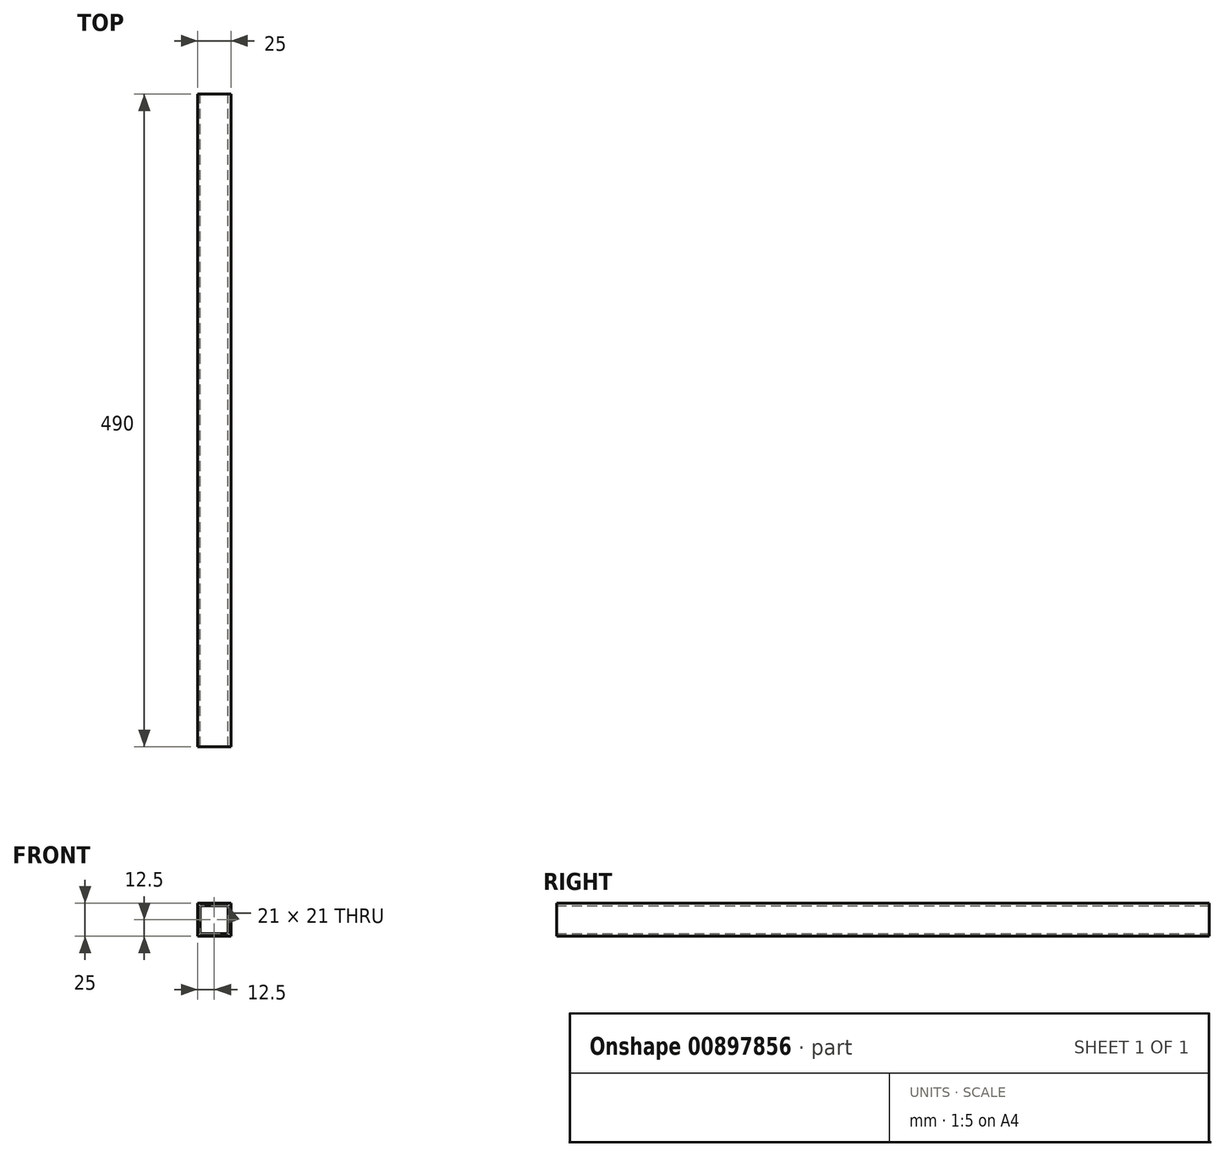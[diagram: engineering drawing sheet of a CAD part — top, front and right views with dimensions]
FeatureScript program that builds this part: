
annotation { "Feature Type Name" : "Feature", "Feature Type Description" : "" }
export const myFeature = defineFeature(function(context is Context, id is Id, definition is map)
    precondition{}
    {
        {
            var Q0;
            Q0=qCreatedBy(makeId("Front.planeOp"),FACE);
            var sketch = newSketch(context, id + "F0", { "sketchPlane" : qUnion([Q0])});
            skLineSegment(sketch, "E0.bottom", {"start": v(12.5, -12.5) * mm, "end": v(-12.5, -12.5) * mm});
            skLineSegment(sketch, "E0.top", {"start": v(12.5, 12.5) * mm, "end": v(-12.5, 12.5) * mm});
            skLineSegment(sketch, "E0.left", {"start": v(12.5, -12.5) * mm, "end": v(12.5, 12.5) * mm});
            skLineSegment(sketch, "E0.right", {"start": v(-12.5, -12.5) * mm, "end": v(-12.5, 12.5) * mm});
            skPoint(sketch, "E0.middle", {"position": v(0, 0) * mm});
            skLineSegment(sketch, "E1.0", {"start": v(10.5, 10.5) * mm, "end": v(-10.5, 10.5) * mm});
            skLineSegment(sketch, "E1.1", {"start": v(10.5, -10.5) * mm, "end": v(10.5, 10.5) * mm});
            skLineSegment(sketch, "E1.2", {"start": v(10.5, -10.5) * mm, "end": v(-10.5, -10.5) * mm});
            skLineSegment(sketch, "E1.3", {"start": v(-10.5, -10.5) * mm, "end": v(-10.5, 10.5) * mm});
            skSolve(sketch);
        }
        {
            var Q0;
            Q0=qSketchRegion(id+"F0",true);
            extrude(context, id + "F1", {"entities" : qUnion([Q0]), "depth" : 245 * mm, "offsetDistance" : 25 * mm, "hasSecondDirection" : true, "secondDirectionOppositeDirection" : true, "secondDirectionDepth" : 245 * mm});
        }
    });
